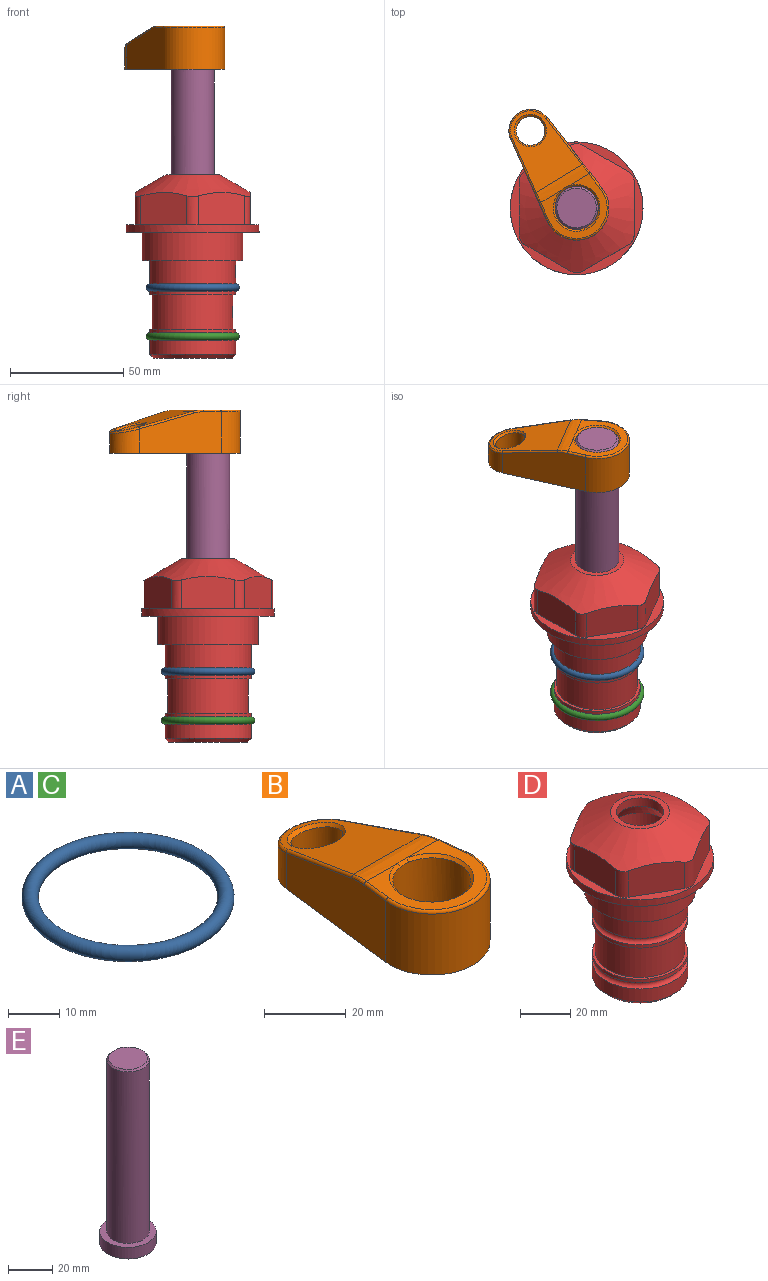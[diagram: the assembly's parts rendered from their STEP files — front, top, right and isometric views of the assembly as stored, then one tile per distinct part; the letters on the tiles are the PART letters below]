
ASSEMBLY  parts=5 mates=4
PART A: 1 faces, bbox 44.7x44.7x3.2 mm
  f0: torus R=19.05mm, axis (0,0,1), area 1193.9mm2
PART B: 31 faces, bbox 31.7x65.5x19.8 mm
  f0: plane 39.12x18.26mm, normal (0.99,0.12,0), area 612.2mm2, adj f1,f4,f7,f11,f13,f15
  f1: cylinder r=9.53mm len=18.91mm, axis (0,0,-1), area 296.1mm2, adj f0,f2,f7,f17
  f2: plane 39.12x18.26mm, normal (-0.99,0.12,0), area 612.2mm2, adj f1,f4,f7,f12,f14,f16
  f3: cylinder r=6.35mm len=12.7mm, axis (0,0,-1), area 362.4mm2, adj f7,f18
  f4: cylinder r=14.29mm len=28.58mm, axis (0,0,-1), area 882.2mm2, adj f0,f2,f7,f10
  f5: cylinder r=9.53mm len=19.05mm, axis (0,0,-1), area 1092.6mm2, adj f7,f19,f20
  f6: plane 26.99x23.69mm, normal (0,0,1), area 216.2mm2, adj f9,f10,f11,f12,f19
  f7: plane 63.5x28.58mm, normal (0,0,-1), area 661.8mm2, adj f0,f1,f2,f3,f4,f5,f22,f23
  f8: plane 33.52x23.6mm, normal (0,0.26,0.97), area 486mm2, adj f9,f15,f16,f17,f18
  f9: cylinder r=19.05mm len=24.72mm, axis (1,0,0), area 120.4mm2, adj f6,f8,f13,f14,f20
  f10: torus R=13.49mm, axis (0,0,1), area 59mm2, adj f4,f6,f11,f12
  f11: cylinder r=0.79mm len=8.67mm, axis (0.12,-0.99,0), area 10.8mm2, adj f0,f6,f10,f13
  f12: cylinder r=0.79mm len=8.67mm, axis (0.12,0.99,0), area 10.8mm2, adj f2,f6,f10,f14
  f13: bspline ~4.95x1.42mm, area 6.1mm2, adj f0,f9,f11,f15
  f14: bspline ~4.95x1.42mm, area 6.1mm2, adj f2,f9,f12,f16
  f15: cylinder r=0.79mm len=25.95mm, axis (0.12,-0.96,0.26), area 32.9mm2, adj f0,f8,f13,f17
  f16: cylinder r=0.79mm len=25.95mm, axis (0.12,0.96,-0.26), area 32.9mm2, adj f2,f8,f14,f17
  f17: bspline ~18.91x8.38mm, area 30mm2, adj f1,f8,f15,f16
  f18: bspline ~14.29x14.29mm, area 48.3mm2, adj f3,f8
  f19: cone r=9.53mm half-angle=45deg, axis (0,0,1), area 66.5mm2, adj f5,f6,f20
  f20: bspline ~3.22x0.96mm, area 3.5mm2, adj f5,f9,f19
  f21: plane 2.75x2.72mm, normal (0,0,-1), area 2.9mm2, adj f23,f25,f28
  f22: plane 23.05x15.88mm, normal (-0.99,-0.12,0), area 323.6mm2, adj f7,f25,f26,f27,f28,f29
  f23: plane 23.05x15.88mm, normal (0.99,-0.12,0), area 323.6mm2, adj f7,f21,f25,f27,f28,f30
  f24: cylinder r=9.53mm len=10.69mm, axis (0,0,-1), area 114.7mm2, adj f7,f27,f29,f30
  f25: cylinder r=12.7mm len=20.59mm, axis (0,0,-1), area 381.1mm2, adj f7,f21,f22,f23,f26,f28
  f26: plane 2.75x2.72mm, normal (0,0,-1), area 2.9mm2, adj f22,f25,f28
  f27: plane 19.72x18.37mm, normal (0,-0.26,-0.97), area 291.8mm2, adj f22,f23,f24,f28,f29,f30
  f28: cylinder r=15.88mm len=19.92mm, axis (1,0,0), area 54.8mm2, adj f21,f22,f23,f25,f26,f27
  f29: cylinder r=1.59mm len=11mm, axis (0,0,-1), area 34.7mm2, adj f7,f22,f24,f27
  f30: cylinder r=1.59mm len=11mm, axis (0,0,-1), area 34.7mm2, adj f7,f23,f24,f27
PART C: same geometry as A
PART D: 36 faces, bbox 58.7x58.7x81 mm
  f0: cylinder r=17.78mm len=35.56mm, axis (0,0,1), area 1670.8mm2, adj f23,f24,f31
  f1: cylinder r=19.05mm len=38.1mm, axis (0,0,1), area 1191.9mm2, adj f26,f27,f30
  f2: plane 58.66x58.66mm, normal (0,0,-1), area 1150.6mm2, adj f3,f28
  f3: cylinder r=29.33mm len=58.66mm, axis (0,0,-1), area 585.1mm2, adj f2,f4
  f4: plane 58.66x58.66mm, normal (0,0,1), area 475.9mm2, adj f3,f5,f6,f7,f8,f9,f10,f11
  f5: plane 20.32x14.34mm, normal (-0.5,0.87,0), area 324.4mm2, adj f4,f15,f16,f17
  f6: plane 20.32x14.34mm, normal (0.5,0.87,0), area 324.4mm2, adj f4,f14,f15,f17
  f7: plane 23.48x14.34mm, normal (1,0,0), area 324.4mm2, adj f4,f13,f14,f17
  f8: plane 20.32x14.34mm, normal (0.5,-0.87,0), area 324.4mm2, adj f4,f12,f13,f17
  f9: plane 20.32x14.34mm, normal (-0.5,-0.87,0), area 324.4mm2, adj f4,f11,f12,f17
  f10: plane 23.48x14.34mm, normal (-1,0,0), area 324.4mm2, adj f4,f11,f16,f17
  f11: cylinder r=5.08mm len=12.85mm, axis (0,0,-1), area 67.2mm2, adj f4,f9,f10,f17
  f12: cylinder r=5.08mm len=12.85mm, axis (0,0,-1), area 67.2mm2, adj f4,f8,f9,f17
  f13: cylinder r=5.08mm len=12.85mm, axis (0,0,-1), area 67.2mm2, adj f4,f7,f8,f17
  f14: cylinder r=5.08mm len=12.85mm, axis (0,0,-1), area 67.2mm2, adj f4,f6,f7,f17
  f15: cylinder r=5.08mm len=12.85mm, axis (0,0,-1), area 67.2mm2, adj f4,f5,f6,f17
  f16: cylinder r=5.08mm len=12.85mm, axis (0,0,-1), area 67.2mm2, adj f4,f5,f10,f17
  f17: cone r=11.73mm half-angle=60deg, axis (0,0,-1), area 2071.8mm2, adj f5,f6,f7,f8,f9,f10,f11,f12
  f18: plane 23.46x23.46mm, normal (0,0,1), area 147.4mm2, adj f17,f35
  f19: plane 34.93x34.93mm, normal (0,0,-1), area 958mm2, adj f29
  f20: cylinder r=19.05mm len=38.1mm, axis (0,0,1), area 760.1mm2, adj f21,f29
  f21: torus R=19.05mm, axis (0,0,1), area 565.3mm2, adj f20,f22
  f22: cylinder r=19.05mm len=38.1mm, axis (0,0,1), area 190mm2, adj f21,f23
  f23: plane 38.1x38.1mm, normal (0,0,1), area 146.9mm2, adj f0,f22
  f24: plane 38.1x38.1mm, normal (0,0,-1), area 146.9mm2, adj f0,f25
  f25: cylinder r=19.05mm len=38.1mm, axis (0,0,1), area 190mm2, adj f24,f26
  f26: torus R=19.05mm, axis (0,0,1), area 565.3mm2, adj f1,f25
  f27: plane 44.45x44.45mm, normal (0,0,-1), area 411.7mm2, adj f1,f28
  f28: cylinder r=22.23mm len=44.45mm, axis (0,0,1), area 1773.5mm2, adj f2,f27
  f29: cone r=19.05mm half-angle=45deg, axis (0,0,1), area 257.5mm2, adj f19,f20
  f30: cylinder r=3.17mm len=6.75mm, axis (-1,0,0), area 128mm2, adj f1,f33
  f31: cylinder r=3.17mm len=6.35mm, axis (-1,0,0), area 102.5mm2, adj f0,f33
  f32: plane 25.4x25.4mm, normal (0,0,1), area 506.7mm2, adj f33
  f33: cylinder r=12.7mm len=66.42mm, axis (0,0,-1), area 5236.2mm2, adj f30,f31,f32,f34
  f34: cone r=9.53mm half-angle=30deg, axis (0,0,-1), area 443.4mm2, adj f33,f35
  f35: cylinder r=9.53mm len=19.05mm, axis (0,0,-1), area 240.9mm2, adj f18,f34
PART E: 6 faces, bbox 25.4x25.4x101.6 mm
  f0: plane 17.46x17.46mm, normal (0,0,1), area 239.5mm2, adj f5
  f1: plane 25.4x25.4mm, normal (0,0,-1), area 506.7mm2, adj f2
  f2: cylinder r=12.7mm len=25.4mm, axis (0,0,1), area 506.7mm2, adj f1,f3
  f3: plane 25.4x25.4mm, normal (0,0,1), area 221.7mm2, adj f2,f4
  f4: cylinder r=9.53mm len=94.46mm, axis (0,0,1), area 5653mm2, adj f3,f5
  f5: cone r=8.73mm half-angle=45deg, axis (0,0,-1), area 64.4mm2, adj f0,f4
PLACE A at identity
PLACE B rot(axis=(0,0,1),30.9deg) t=(0,0,27.55)mm
PLACE C t=(0,0,-21.59)mm
PLACE D at identity fixed
PLACE E rot(axis=(0,0,1),30.9deg) t=(0,0,27.55)mm
MATE fastened C.f0 <-> D.f0  axis (0,0,1) through (0,0,-46.1)mm
MATE fastened A.f0 <-> D.f0  axis (0,0,1) through (0,0,-24.51)mm
MATE fastened B.f4 <-> E.f2  axis (0,0,1) through (0,0,91.05)mm
MATE cylindrical D.f0 <-> E.f2  axis (0,0,1) through (0,0,-50.55)mm
